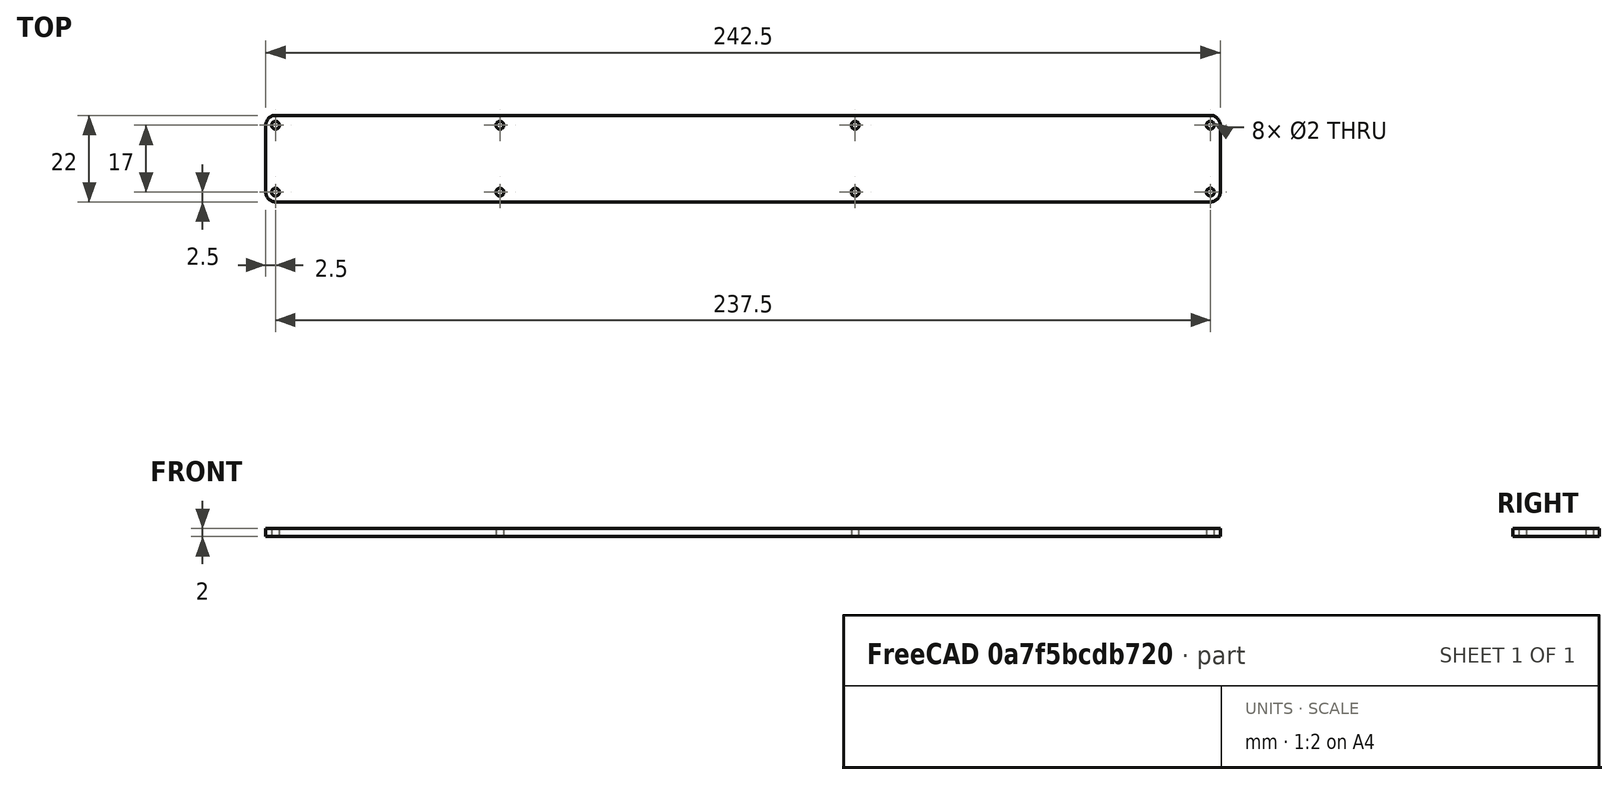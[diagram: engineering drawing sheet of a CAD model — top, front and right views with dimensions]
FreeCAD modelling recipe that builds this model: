
FCSTD DOCUMENT  (FreeCAD 1.0R39285 (Git))
Label: cover-plate
License: All rights reserved
LicenseURL: https://en.wikipedia.org/wiki/All_rights_reserved
objects: Sketcher::SketchObject×2, PartDesign::Pad×1, PartDesign::Body×1
note: 8 computed .brp shape members not serialized (recipe doc carries the construction recipe); baked Part::Feature solids carry a one-line shape summary decoded from their .brp

FEATURE [Sketcher::SketchObject] Sketch
  ArcFitTolerance = 1e-06
  FullyConstrained = true
  MakeInternals = false
FEATURE [Sketcher::SketchObject] Sketch001
  ArcFitTolerance = 1e-06
  AttachmentSupport = -> [XY_Plane]
  FullyConstrained = true
  MakeInternals = false
  MapMode = 5
  sketch-geometry (16):
    g0: LineSegment StartX=-121.25 StartY=-8.5 StartZ=0 EndX=-121.25 EndY=8.5 EndZ=0
    g1: ArcOfCircle CenterX=-118.75 CenterY=8.5 CenterZ=0 NormalX=0 NormalY=0 NormalZ=1 AngleXU=0 Radius=2.5 StartAngle=1.5708 EndAngle=3.14159
    g2: LineSegment StartX=-118.75 StartY=11 StartZ=0 EndX=118.75 EndY=11 EndZ=0
    g3: ArcOfCircle CenterX=118.75 CenterY=8.5 CenterZ=0 NormalX=0 NormalY=0 NormalZ=1 AngleXU=0 Radius=2.5 StartAngle=1.2e-15 EndAngle=1.5708
    g4: LineSegment StartX=121.25 StartY=8.5 StartZ=0 EndX=121.25 EndY=-8.5 EndZ=0
    g5: ArcOfCircle CenterX=118.75 CenterY=-8.5 CenterZ=0 NormalX=0 NormalY=0 NormalZ=1 AngleXU=0 Radius=2.5 StartAngle=4.71239 EndAngle=6.28319
    g6: LineSegment StartX=118.75 StartY=-11 StartZ=0 EndX=-118.75 EndY=-11 EndZ=0
    g7: ArcOfCircle CenterX=-118.75 CenterY=-8.5 CenterZ=0 NormalX=0 NormalY=0 NormalZ=1 AngleXU=0 Radius=2.5 StartAngle=3.14159 EndAngle=4.71239
    g8: Circle CenterX=-118.75 CenterY=8.5 CenterZ=0 NormalX=0 NormalY=0 NormalZ=1 AngleXU=0 Radius=1
    g9: Circle CenterX=-61.75 CenterY=8.5 CenterZ=0 NormalX=0 NormalY=0 NormalZ=1 AngleXU=0 Radius=1
    g10: Circle CenterX=28.5 CenterY=8.5 CenterZ=0 NormalX=0 NormalY=0 NormalZ=1 AngleXU=0 Radius=1
    g11: Circle CenterX=118.75 CenterY=8.5 CenterZ=0 NormalX=0 NormalY=0 NormalZ=1 AngleXU=0 Radius=1
    g12: Circle CenterX=-118.75 CenterY=-8.5 CenterZ=0 NormalX=0 NormalY=0 NormalZ=1 AngleXU=0 Radius=1
    g13: Circle CenterX=-61.75 CenterY=-8.5 CenterZ=0 NormalX=0 NormalY=0 NormalZ=1 AngleXU=0 Radius=1
    g14: Circle CenterX=28.5 CenterY=-8.5 CenterZ=0 NormalX=0 NormalY=0 NormalZ=1 AngleXU=0 Radius=1
    g15: Circle CenterX=118.75 CenterY=-8.5 CenterZ=0 NormalX=0 NormalY=0 NormalZ=1 AngleXU=0 Radius=1
  constraints (43):
    c: Tangent(g0,g1) = 1.5708
    c: Tangent(g1,g2) = 1.5708
    c: Tangent(g2,g3) = 1.5708
    c: Tangent(g3,g4) = 1.5708
    c: Tangent(g4,g5) = 1.5708
    c: Tangent(g5,g6) = 1.5708
    c: Tangent(g6,g7) = 1.5708
    c: Tangent(g7,g0) = 1.5708
    c: Vertical(g0)
    c: Vertical(g4)
    c: Horizontal(g2)
    c: Horizontal(g6)
    c: Radius(g1) = 2.5
    c: Radius(g3) = 2.5
    c: Radius(g5) = 2.5
    c: Radius(g7) = 2.5
    c: Symmetric(g1,g5,g-1)
    c: Distance(g4,g0) = 242.5
    c: Distance(g6,g2) = 22
    c: Diameter(g8) = 2
    c: Diameter(g9) = 2
    c: Diameter(g10) = 2
    c: Diameter(g11) = 2
    c: Diameter(g12) = 2
    c: Diameter(g13) = 2
    c: Diameter(g14) = 2
    c: Diameter(g15) = 2
    c: Distance(g8,g2) = 2.5
    c: Distance(g8,g0) = 2.5
    c: Distance(g11,g4) = 2.5
    c: Distance(g9,g0) = 59.5
    c: Distance(g12,g2) = 19.5
    c: Horizontal(g1,g9)
    c: Horizontal(g9,g10)
    c: Horizontal(g10,g11)
    c: Vertical(g1,g12)
    c: Vertical(g13,g9)
    c: Horizontal(g12,g13)
    c: Distance(g10,g4) = 92.75
    c: Vertical(g3,g15)
    c: Horizontal(g15,g13)
    c: Horizontal(g13,g14)
    c: Vertical(g10,g14)
FEATURE [PartDesign::Pad] Pad
  Direction = (0,0,1)
  Length = 2
  Length2 = 10
  Profile = -> Sketch001
  ReferenceAxis = -> Sketch001 [N_Axis]
  Refine = true
  Suppressed = false
  Type = 0
FEATURE [PartDesign::Body] Body
  AllowCompound = false
  Group = -> [Sketch001,Pad]
  Origin = -> Origin
  Tip = -> Pad
